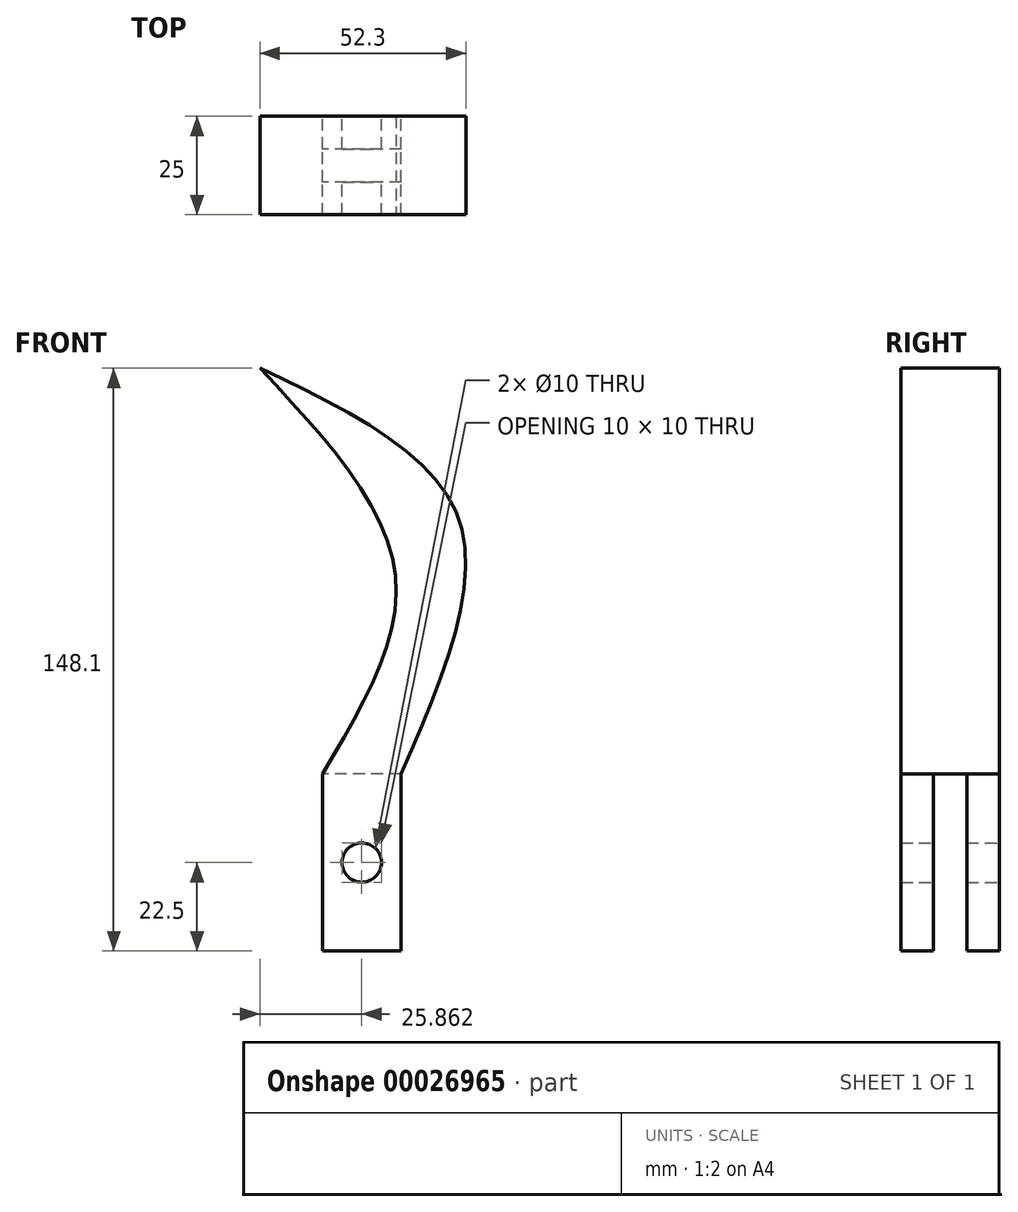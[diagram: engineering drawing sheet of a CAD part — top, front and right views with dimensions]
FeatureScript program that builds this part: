
annotation { "Feature Type Name" : "Feature", "Feature Type Description" : "" }
export const myFeature = defineFeature(function(context is Context, id is Id, definition is map)
    precondition{}
    {
        {
            var Q0;
            Q0=qCreatedBy(makeId("Front.planeOp"),FACE);
            var sketch = newSketch(context, id + "F0", { "sketchPlane" : qUnion([Q0])});
            skFitSpline(sketch, "E0", {"points": [v(0, 103.1) * mm, v(50.34, 65.17) * mm, v(35.86, 0) * mm], "startDerivative": vector(134.37, -64.27) * mm, "endDerivative": vector(-61.7, -141.57) * mm});
            skLineSegment(sketch, "E1", {"start": v(35.86, 0) * mm, "end": v(35.86, -45) * mm});
            skLineSegment(sketch, "E2", {"start": v(35.86, -45) * mm, "end": v(15.86, -45) * mm});
            skLineSegment(sketch, "E3", {"start": v(15.86, -45) * mm, "end": v(15.86, 0) * mm});
            skCircle(sketch, "E4", {"center": v(25.86, -22.5) * mm, "radius": 5 * mm});
            skFitSpline(sketch, "E5", {"points": [v(15.86, 0) * mm, v(34.4, 50.8) * mm, v(0, 103.1) * mm], "startDerivative": vector(63.71, 106.55) * mm, "endDerivative": vector(-93.52, 99.74) * mm});
            skSolve(sketch);
        }
        {
            var Q0;
            Q0=makeQuery(id+"F0.imprint","IMPRINT",FACE,{"disambiguationData":[TD([[makeQuery(id+"F0.imprint","IMPRINT",EDGE,{"derivedFrom":sQuery(id+"F0.wireOp",EDGE,"E0")}),-1.0]])]});
            extrude(context, id + "F1", {"entities" : qUnion([Q0]), "depth" : 25 * mm});
        }
        {
            var Q0;
            Q0=makeQuery(id+"F1.opExtrude","SWEPT_FACE",FACE,{"disambiguationData":[OSD([sQuery(id+"F0.wireOp",EDGE,"E3")])]});
            var sketch = newSketch(context, id + "F2", { "sketchPlane" : qUnion([Q0])});
            skLineSegment(sketch, "E6", {"start": v(0, 0) * mm, "end": v(25, 0) * mm});
            skLineSegment(sketch, "E7", {"start": v(8.3, 0) * mm, "end": v(8.3, -45) * mm});
            skLineSegment(sketch, "E8", {"start": v(16.7, 0) * mm, "end": v(16.7, -45) * mm});
            skSolve(sketch);
        }
        {
            var Q0;
            {var subQ2=sQuery(id+"F2.wireOp",EDGE,"E7");Q0=makeQuery(id+"F2.imprint","IMPRINT",FACE,{"disambiguationData":[TD([[makeQuery(id+"F2.imprint","IMPRINT",EDGE,{"derivedFrom":subQ2}),1.0]])]});}
            extrude(context, id + "F3", {"entities" : qUnion([Q0]), "operationType" : NewBodyOperationType.REMOVE, "endBound" : BoundingType.THROUGH_ALL, "oppositeDirection" : true, "depth" : 25 * mm});
        }
    });
